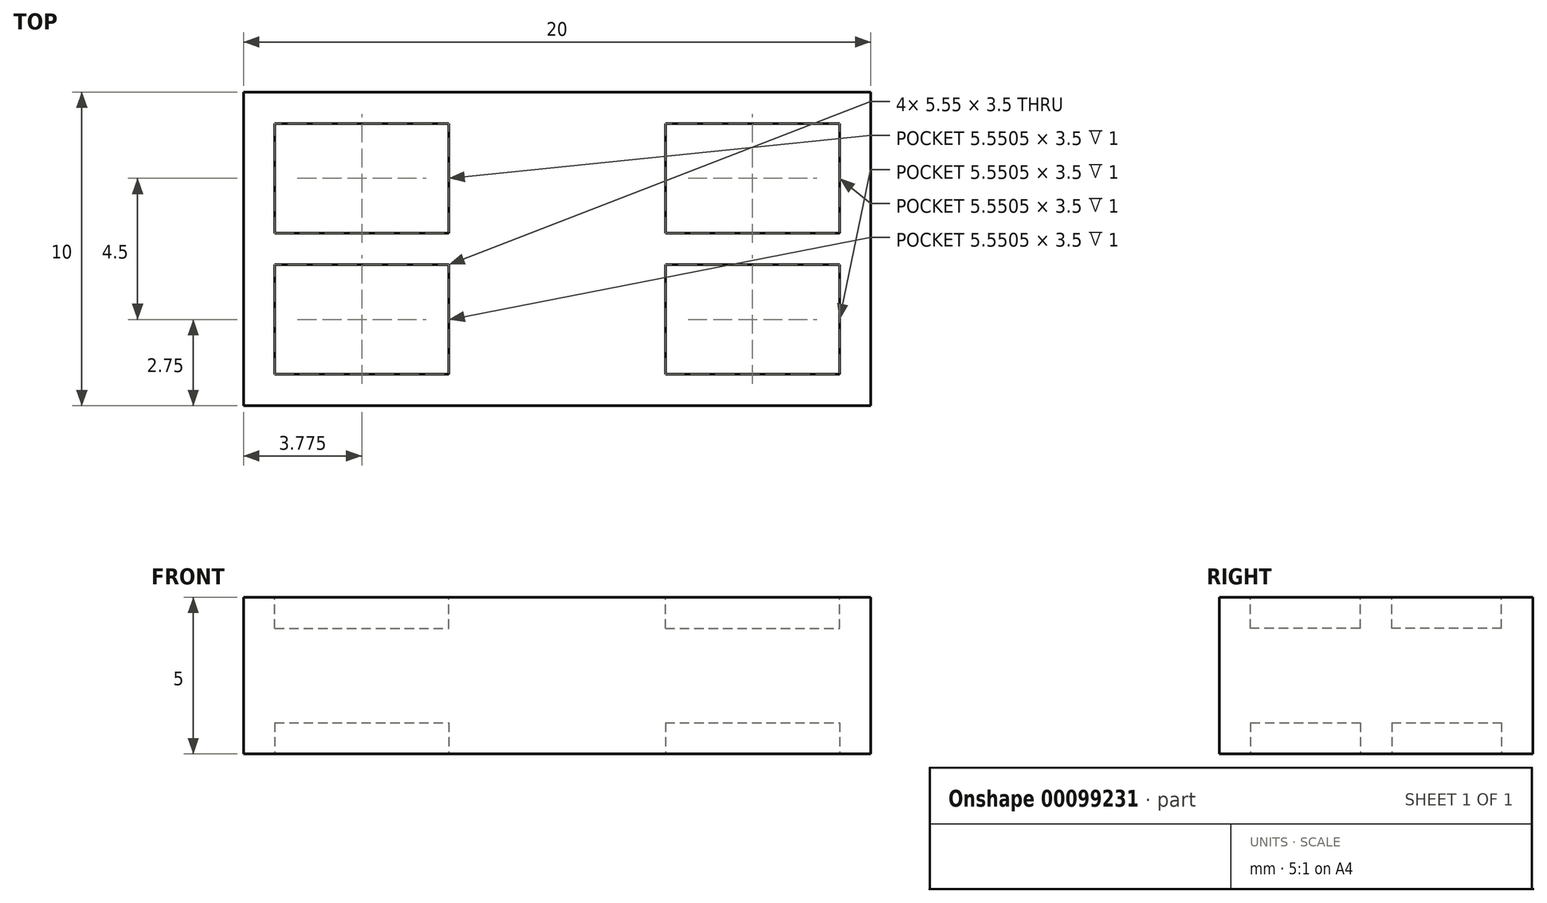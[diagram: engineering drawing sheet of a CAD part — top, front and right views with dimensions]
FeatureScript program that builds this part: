
annotation { "Feature Type Name" : "Feature", "Feature Type Description" : "" }
export const myFeature = defineFeature(function(context is Context, id is Id, definition is map)
    precondition{}
    {
        {
            var Q0;
            Q0=qCreatedBy(makeId("Top.planeOp"),FACE);
            var sketch = newSketch(context, id + "F0", { "sketchPlane" : qUnion([Q0])});
            skLineSegment(sketch, "E0.bottom", {"start": v(0, 0) * mm, "end": v(20, 0) * mm});
            skLineSegment(sketch, "E0.top", {"start": v(0, -10) * mm, "end": v(20, -10) * mm});
            skLineSegment(sketch, "E0.left", {"start": v(0, 0) * mm, "end": v(0, -10) * mm});
            skLineSegment(sketch, "E0.right", {"start": v(20, 0) * mm, "end": v(20, -10) * mm});
            skLineSegment(sketch, "E1", {"start": v(10, 0) * mm, "end": v(10, -10) * mm, "construction": true});
            skSolve(sketch);
        }
        {
            var Q0;
            Q0=makeQuery(id+"F0.imprint","IMPRINT",FACE,{"disambiguationData":[TD([[makeQuery(id+"F0.imprint","IMPRINT",EDGE,{"derivedFrom":sQuery(id+"F0.wireOp",EDGE,"E0.bottom")}),-1.0]])]});
            extrude(context, id + "F1", {"entities" : qUnion([Q0]), "depth" : 5 * mm});
        }
        {
            var Q0;
            Q0=makeQuery(id+"F1.opExtrude","SWEPT_FACE",FACE,{"disambiguationData":[OSD([sQuery(id+"F0.wireOp",EDGE,"E0.top")])]});
            var sketch = newSketch(context, id + "F2", { "sketchPlane" : qUnion([Q0])});
            skPoint(sketch, "E2", {"position": v(10, 5) * mm});
            skLineSegment(sketch, "E3", {"start": v(10, 5) * mm, "end": v(10, 0) * mm, "construction": true});
            skPoint(sketch, "E4", {"position": v(10, 2.5) * mm});
            skCircle(sketch, "E5", {"center": v(10, 2.5) * mm, "radius": 3.5 * mm});
            skSolve(sketch);
        }
        {
            var Q0;
            {var subQ0=sQuery(id+"F2.wireOp",EDGE,"E5");var subQ1=makeQuery(id+"F1.opExtrude","CAP_EDGE",EDGE,{"disambiguationData":[OSD([sQuery(id+"F0.wireOp",EDGE,"E0.top")])],"isStart":false});var subQ2=makeQuery(id+"F2.imprint","INTERSECT",VERTEX,{"disambiguationData":[OD(0.0)],"derivedFrom":[subQ1,subQ0]});Q0=makeQuery(id+"F2.imprint","IMPRINT",FACE,{"disambiguationData":[TD([[makeQuery(id+"F2.imprint","IMPRINT",EDGE,{"disambiguationData":[TD([[subQ2,1.0]])],"derivedFrom":subQ0}),1.0]])]});}
            var Q1;
            {var subQ0=sQuery(id+"F2.wireOp",EDGE,"E5");var subQ1=makeQuery(id+"F1.opExtrude","CAP_EDGE",EDGE,{"disambiguationData":[OSD([sQuery(id+"F0.wireOp",EDGE,"E0.top")])],"isStart":true});var subQ2=makeQuery(id+"F2.imprint","INTERSECT",VERTEX,{"disambiguationData":[OD(0.0)],"derivedFrom":[subQ1,subQ0]});Q1=makeQuery(id+"F2.imprint","IMPRINT",FACE,{"disambiguationData":[TD([[makeQuery(id+"F2.imprint","IMPRINT",EDGE,{"disambiguationData":[TD([[subQ2,-1.0]])],"derivedFrom":subQ0}),1.0]])]});}
            extrude(context, id + "F3", {"entities" : qUnion([Q0, Q1]), "operationType" : NewBodyOperationType.ADD, "oppositeDirection" : true, "depth" : 10 * mm});
        }
        {
            var Q0;
            {var subQ0=sQuery(id+"F0.wireOp",EDGE,"E0.left");var subQ2=sQuery(id+"F0.wireOp",EDGE,"E0.top");var subQ8=sQuery(id+"F0.wireOp",EDGE,"E0.bottom");Q0=makeQuery(id+"F3.boolean.opBoolean","SPLIT",FACE,{"disambiguationData":[TD([makeQuery(id+"F1.opExtrude","SWEPT_FACE",FACE,{"disambiguationData":[OSD([subQ0])]})])],"derivedFrom":makeQuery(id+"F1.opExtrude","CAP_FACE",FACE,{"disambiguationData":[OSD([subQ8,subQ2,subQ0,sQuery(id+"F0.wireOp",EDGE,"E0.right")])],"isStart":false})});}
            var sketch = newSketch(context, id + "F4", { "sketchPlane" : qUnion([Q0])});
            skLineSegment(sketch, "E6.bottom", {"start": v(1, -1) * mm, "end": v(6.55, -1) * mm});
            skLineSegment(sketch, "E6.top", {"start": v(1, -4.5) * mm, "end": v(6.55, -4.5) * mm});
            skLineSegment(sketch, "E6.left", {"start": v(1, -1) * mm, "end": v(1, -4.5) * mm});
            skLineSegment(sketch, "E6.right", {"start": v(6.55, -1) * mm, "end": v(6.55, -4.5) * mm});
            skLineSegment(sketch, "E7.bottom", {"start": v(1, -5.5) * mm, "end": v(6.55, -5.5) * mm});
            skLineSegment(sketch, "E7.top", {"start": v(1, -9) * mm, "end": v(6.55, -9) * mm});
            skLineSegment(sketch, "E7.left", {"start": v(1, -5.5) * mm, "end": v(1, -9) * mm});
            skLineSegment(sketch, "E7.right", {"start": v(6.55, -5.5) * mm, "end": v(6.55, -9) * mm});
            skLineSegment(sketch, "E8.bottom", {"start": v(13.45, -1) * mm, "end": v(19, -1) * mm});
            skLineSegment(sketch, "E8.top", {"start": v(13.45, -4.5) * mm, "end": v(19, -4.5) * mm});
            skLineSegment(sketch, "E8.left", {"start": v(13.45, -1) * mm, "end": v(13.45, -4.5) * mm});
            skLineSegment(sketch, "E8.right", {"start": v(19, -1) * mm, "end": v(19, -4.5) * mm});
            skPoint(sketch, "E9.firstSnap0", {"position": v(13.45, -2.75) * mm});
            skLineSegment(sketch, "E9.bottom", {"start": v(13.45, -5.5) * mm, "end": v(19, -5.5) * mm});
            skLineSegment(sketch, "E9.top", {"start": v(13.45, -9) * mm, "end": v(19, -9) * mm});
            skLineSegment(sketch, "E9.left", {"start": v(13.45, -5.5) * mm, "end": v(13.45, -9) * mm});
            skLineSegment(sketch, "E9.right", {"start": v(19, -5.5) * mm, "end": v(19, -9) * mm});
            skSolve(sketch);
        }
        {
            var Q0;
            Q0=makeQuery(id+"F4.imprint","IMPRINT",FACE,{"disambiguationData":[TD([[makeQuery(id+"F4.imprint","IMPRINT",EDGE,{"derivedFrom":sQuery(id+"F4.wireOp",EDGE,"E6.bottom")}),-1.0]])]});
            var Q1;
            Q1=makeQuery(id+"F4.imprint","IMPRINT",FACE,{"disambiguationData":[TD([[makeQuery(id+"F4.imprint","IMPRINT",EDGE,{"derivedFrom":sQuery(id+"F4.wireOp",EDGE,"E7.bottom")}),-1.0]])]});
            var Q2;
            Q2=makeQuery(id+"F4.imprint","IMPRINT",FACE,{"disambiguationData":[TD([[makeQuery(id+"F4.imprint","IMPRINT",EDGE,{"derivedFrom":sQuery(id+"F4.wireOp",EDGE,"E8.bottom")}),-1.0]])]});
            var Q3;
            Q3=makeQuery(id+"F4.imprint","IMPRINT",FACE,{"disambiguationData":[TD([[makeQuery(id+"F4.imprint","IMPRINT",EDGE,{"derivedFrom":sQuery(id+"F4.wireOp",EDGE,"E9.bottom")}),-1.0]])]});
            extrude(context, id + "F5", {"entities" : qUnion([Q0, Q1, Q2, Q3]), "operationType" : NewBodyOperationType.REMOVE, "oppositeDirection" : true, "depth" : 1 * mm});
        }
        {
            var Q0;
            {var subQ0=sQuery(id+"F0.wireOp",EDGE,"E0.right");var subQ1=sQuery(id+"F0.wireOp",EDGE,"E0.top");var subQ8=sQuery(id+"F0.wireOp",EDGE,"E0.bottom");Q0=makeQuery(id+"F3.boolean.opBoolean","SPLIT",FACE,{"disambiguationData":[TD([makeQuery(id+"F1.opExtrude","SWEPT_FACE",FACE,{"disambiguationData":[OSD([subQ0])]})])],"derivedFrom":makeQuery(id+"F1.opExtrude","CAP_FACE",FACE,{"disambiguationData":[OSD([subQ8,subQ1,sQuery(id+"F0.wireOp",EDGE,"E0.left"),subQ0])],"isStart":true})});}
            var sketch = newSketch(context, id + "F6", { "sketchPlane" : qUnion([Q0])});
            skLineSegment(sketch, "E10.bottom", {"start": v(1, 9) * mm, "end": v(6.55, 9) * mm});
            skLineSegment(sketch, "E10.top", {"start": v(1, 5.5) * mm, "end": v(6.55, 5.5) * mm});
            skLineSegment(sketch, "E10.left", {"start": v(1, 9) * mm, "end": v(1, 5.5) * mm});
            skLineSegment(sketch, "E10.right", {"start": v(6.55, 9) * mm, "end": v(6.55, 5.5) * mm});
            skPoint(sketch, "E11", {"position": v(20, 5) * mm});
            skLineSegment(sketch, "E12.bottom", {"start": v(1, 4.5) * mm, "end": v(6.55, 4.5) * mm});
            skLineSegment(sketch, "E12.top", {"start": v(1, 1) * mm, "end": v(6.55, 1) * mm});
            skLineSegment(sketch, "E12.left", {"start": v(1, 4.5) * mm, "end": v(1, 1) * mm});
            skLineSegment(sketch, "E12.right", {"start": v(6.55, 4.5) * mm, "end": v(6.55, 1) * mm});
            skLineSegment(sketch, "E13.bottom", {"start": v(13.45, 9) * mm, "end": v(19, 9) * mm});
            skLineSegment(sketch, "E13.top", {"start": v(13.45, 5.5) * mm, "end": v(19, 5.5) * mm});
            skLineSegment(sketch, "E13.left", {"start": v(13.45, 9) * mm, "end": v(13.45, 5.5) * mm});
            skLineSegment(sketch, "E13.right", {"start": v(19, 9) * mm, "end": v(19, 5.5) * mm});
            skLineSegment(sketch, "E14.bottom", {"start": v(13.45, 4.5) * mm, "end": v(19, 4.5) * mm});
            skLineSegment(sketch, "E14.top", {"start": v(13.45, 1) * mm, "end": v(19, 1) * mm});
            skLineSegment(sketch, "E14.left", {"start": v(13.45, 4.5) * mm, "end": v(13.45, 1) * mm});
            skLineSegment(sketch, "E14.right", {"start": v(19, 4.5) * mm, "end": v(19, 1) * mm});
            skSolve(sketch);
        }
        {
            var Q0;
            Q0=makeQuery(id+"F6.imprint","IMPRINT",FACE,{"disambiguationData":[TD([[makeQuery(id+"F6.imprint","IMPRINT",EDGE,{"derivedFrom":sQuery(id+"F6.wireOp",EDGE,"E10.bottom")}),-1.0]])]});
            var Q1;
            Q1=makeQuery(id+"F6.imprint","IMPRINT",FACE,{"disambiguationData":[TD([[makeQuery(id+"F6.imprint","IMPRINT",EDGE,{"derivedFrom":sQuery(id+"F6.wireOp",EDGE,"E13.bottom")}),-1.0]])]});
            var Q2;
            Q2=makeQuery(id+"F6.imprint","IMPRINT",FACE,{"disambiguationData":[TD([[makeQuery(id+"F6.imprint","IMPRINT",EDGE,{"derivedFrom":sQuery(id+"F6.wireOp",EDGE,"E14.bottom")}),-1.0]])]});
            var Q3;
            Q3=makeQuery(id+"F6.imprint","IMPRINT",FACE,{"disambiguationData":[TD([[makeQuery(id+"F6.imprint","IMPRINT",EDGE,{"derivedFrom":sQuery(id+"F6.wireOp",EDGE,"E12.bottom")}),-1.0]])]});
            extrude(context, id + "F7", {"entities" : qUnion([Q0, Q1, Q2, Q3]), "operationType" : NewBodyOperationType.REMOVE, "oppositeDirection" : true, "depth" : 1 * mm});
        }
    });
